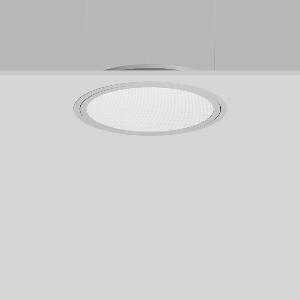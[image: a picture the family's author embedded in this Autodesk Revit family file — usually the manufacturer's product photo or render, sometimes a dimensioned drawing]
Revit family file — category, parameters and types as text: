
# Revit family: triona_round_e_312423_004_1_12_9b29
name_source: partatom
category: Lighting Fixtures
units: mm (PartAtom-declared; Revit-internal decimal feet)

## family parameters
Cut with Voids When Loaded = No
Host = Face
Light Source = No
Part Type = Normal
Room Calculation Point = No
Round Connector Dimension = Use Diameter
Shared = No

## types (1)
- TRIONA round E (1 x LED Modul 840, 3250 lm, 4000)
    Apparent Load = 28 VA
    CIE Flux Codes = 58 87 97 100 100
    Color Rendering = 80
    Color Temperature = 4000
    Default Elevation = 1800 mm
    Description = Series: TRIONA round
Decorative round LED recessed surface luminaire. Cover made of sheet steel, powder-coated. Frame made of aluminium, powder-coated. Recessed ring: aluminium extrusion profile, powder coated. Light emission through a diffuser in plastic, opal/prismatic. Lightguide and diffuser made of non-yellowing plastic (PMMA). Lateral light emission (RZB SIDELITE technology) for above-average homogeneous light distribution. Suitable for installation in cavity ceilings. Tool-free mounting system thanks to the rocker arm mechanism (patent pending). Electronic ballast included. Very easy installation thanks to Plug+Play connection. 
Colour: silver, matt (approx. RAL 9006)
Diameter: 505 mm
Height: 2 mm
Cut-out diameter: 482 mm
Recess height: 100 mm
Luminaire: recess height: 89 mm
Lamp: LED
Socket: without socket
Colour temperature: 4000K
Colour rendering index (CRI): 80
System power: 28 W
Rated luminous flux: 3250 lm
Luminous efficiency: 116 lm/W
Control gear: Converter, dimmable, DALI
Protection class: I
Type of protection: IP 40
    Height = 0 mm  [stored 0 ft]
    Lamp = 1 x LED Modul 840
    Lamp Light Flux = 3250 lm
    Lamp count = 1
    Length = 505 mm
    Lifetime = 50000 h
    Luminous efficacy = 116 lm/W
    Manufacturer = RZB
    ModVariant = No
    Model = 312423.004.1.12
    Mounting Place = Ceiling
    Mounting Type = Recessed
    Number of Poles = 1
    OnlyDefault = Yes
    Power Factor = 1
    Product Name = TRIONA round E
    Product group = Recessed modular luminaires
    ProductGroupID = 406
    Protection Class = Protection class I
    Protection Degree = IP 20
    RLX_Detail_Level = 1
    RLX_Emergency_Light_Flux = 0 lm
    RLX_Emergency_Type = 0
    RLX_Emergency_Type_DB = No
    RlxData = <blob elided: 31693 chars, md5=065397d6>
    Socket = socket
    Standby Power = 0 W
    System Light Flux = 3250 lm
    System Power = 28 W
    Type Comments = Product without accessories
    Type Image = 312423.004.12.jpg
    URL = http://relux.com
    VarID = ---
    Voltage = 230 V
    Voltage Range = 220-240 V
    Weight = 0.00 kg
    Width = 0 mm  [stored 0 ft]

note: [stored X ft] marks values corroborated as IEEE doubles in the binary element streams (Revit-internal decimal feet)

## geometry (parser evidence)
native form markers: Blend x4, Sweep x9
no freeform markers — native parametric forms only
